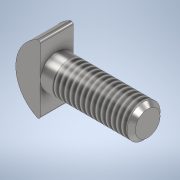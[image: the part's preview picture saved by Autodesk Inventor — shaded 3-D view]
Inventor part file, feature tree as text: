
AUTODESK INVENTOR PART (.ipt)
format: ipt  version: 2021 (Build 250183000, 183)  size: 147,968 bytes
history: native  units: in
note: dims shown in document units (in); Inventor stores cm internally (conversion verified against a paired STEP export)
features: other x2, thread x1
ambient origin geometry x8: Origin, YZ Plane, XZ Plane, XY Plane, X Axis, Y Axis, Z Axis, Center Point
bodies: Body1 (feature_tree)
feature tree (3):
  other  "Sólido2"
  thread  "Rosca1"  [1 undecoded]
  other  "Sólido1"
note: 1 required parameter value undecoded (feature->parameter linkage not recoverable at this tier; creation-order binding heuristic only, values carry confidence <= 0.55)
